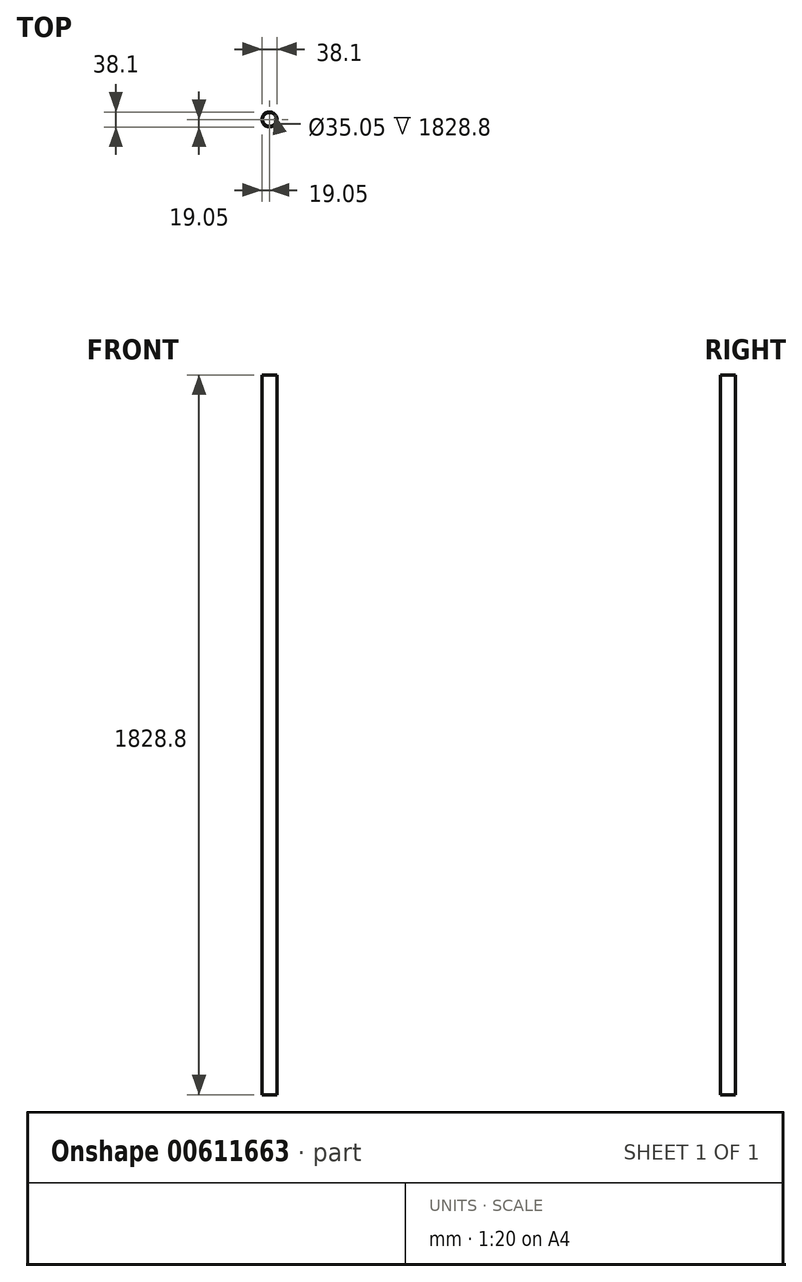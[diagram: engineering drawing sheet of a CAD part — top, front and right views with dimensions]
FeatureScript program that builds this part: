
annotation { "Feature Type Name" : "Feature", "Feature Type Description" : "" }
export const myFeature = defineFeature(function(context is Context, id is Id, definition is map)
    precondition{}
    {
        {
            var Q0;
            Q0=qCreatedBy(makeId("Top.planeOp"),FACE);
            var sketch = newSketch(context, id + "F0", { "sketchPlane" : qUnion([Q0])});
            skCircle(sketch, "E0", {"center": v(0, 0) * mm, "radius": 19.05 * mm});
            skCircle(sketch, "E1", {"center": v(0, 0) * mm, "radius": 17.53 * mm});
            skSolve(sketch);
        }
        {
            var Q0;
            Q0=makeQuery(id+"F0.imprint","IMPRINT",FACE,{"disambiguationData":[TD([[makeQuery(id+"F0.imprint","IMPRINT",EDGE,{"derivedFrom":sQuery(id+"F0.wireOp",EDGE,"E0")}),1.0]])]});
            extrude(context, id + "F1", {"entities" : qUnion([Q0]), "depth" : 1828.8 * mm, "offsetDistance" : 25.4 * mm});
        }
    });
